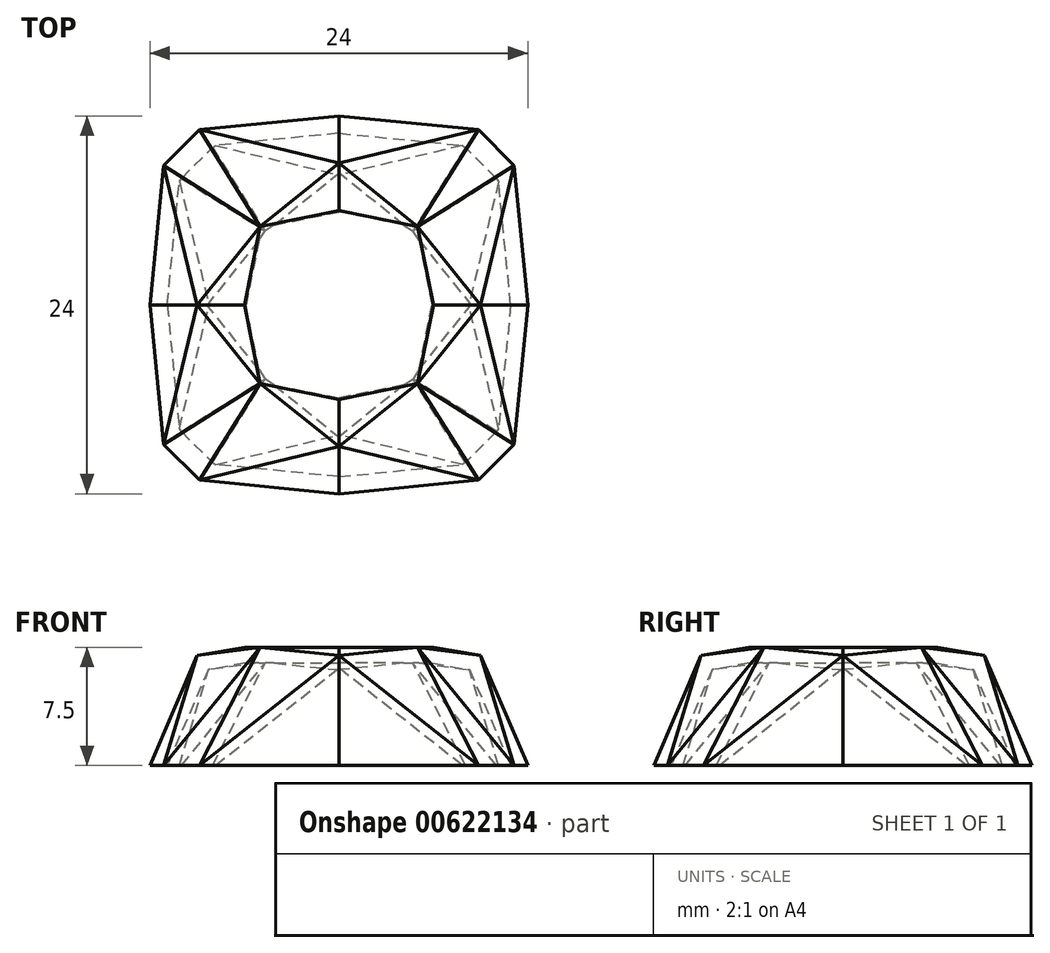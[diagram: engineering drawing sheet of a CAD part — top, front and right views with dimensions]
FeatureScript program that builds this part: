
annotation { "Feature Type Name" : "Feature", "Feature Type Description" : "" }
export const myFeature = defineFeature(function(context is Context, id is Id, definition is map)
    precondition{}
    {
        {
            var Q0;
            Q0=qCreatedBy(makeId("Top.planeOp"),FACE);
            var sketch = newSketch(context, id + "F0", { "sketchPlane" : qUnion([Q0])});
            skLineSegment(sketch, "E0.right", {"start": v(12, 0) * mm, "end": v(12, -12) * mm});
            skLineSegment(sketch, "E1", {"start": v(2, -10) * mm, "end": v(3.15, -11.13) * mm});
            skLineSegment(sketch, "E2", {"start": v(12, -12) * mm, "end": v(3.15, -11.13) * mm});
            skPoint(sketch, "E3.orphan", {"position": v(0, -7.98) * mm});
            skLineSegment(sketch, "E4", {"start": v(12, 0) * mm, "end": v(2, -10) * mm});
            skPoint(sketch, "E5.orphan", {"position": v(0.87, -8.85) * mm});
            skSolve(sketch);
        }
        {
            var Q0;
            Q0=makeQuery(id+"F0.imprint","IMPRINT",FACE,{"disambiguationData":[TD([[makeQuery(id+"F0.imprint","IMPRINT",EDGE,{"derivedFrom":sQuery(id+"F0.wireOp",EDGE,"E0.right")}),-1.0]])]});
            extrude(context, id + "F1", {"entities" : qUnion([Q0]), "depth" : 8.5 * mm, "offsetDistance" : 25.4 * mm});
        }
        {
            var Q0;
            Q0=makeQuery(id+"F1.opExtrude","CAP_FACE",FACE,{"disambiguationData":[OSD([sQuery(id+"F0.wireOp",EDGE,"E0.right"),sQuery(id+"F0.wireOp",EDGE,"E1"),sQuery(id+"F0.wireOp",EDGE,"E2"),sQuery(id+"F0.wireOp",EDGE,"E4")])],"isStart":false});
            var sketch = newSketch(context, id + "F2", { "sketchPlane" : qUnion([Q0])});
            skLineSegment(sketch, "E6", {"start": v(12, 0) * mm, "end": v(7, -5) * mm});
            skLineSegment(sketch, "E7", {"start": v(7, -5) * mm, "end": v(12, -6) * mm});
            skSolve(sketch);
        }
        {
            var Q0;
            {var subQ0=sQuery(id+"F2.wireOp",EDGE,"E6");Q0=makeQuery(id+"F2.imprint","IMPRINT",FACE,{"disambiguationData":[TD([[makeQuery(id+"F2.imprint","IMPRINT",EDGE,{"derivedFrom":subQ0}),1.0]])]});}
            extrude(context, id + "F3", {"entities" : qUnion([Q0]), "operationType" : NewBodyOperationType.REMOVE, "oppositeDirection" : true, "depth" : 1 * mm, "offsetDistance" : 25.4 * mm});
        }
        {
            var Q0;
            Q0=makeQuery(id+"F3.boolean.opBoolean","COPY",EDGE,{"derivedFrom":makeQuery(id+"F3.opExtrude","CAP_EDGE",EDGE,{"disambiguationData":[OSD([sQuery(id+"F2.wireOp",EDGE,"E7")])],"isStart":false})});
            cPlane(context, id + "F4", {"entities" : qUnion([Q0]), "cplaneType" : CPlaneType.LINE_ANGLE, "offset" : 25.4 * mm, "angle" : 100 * degree, "width" : 152.4 * mm, "height" : 152.4 * mm});
        }
        {
            var Q0;
            Q0=qCreatedBy(id+"F4.planeOp",FACE);
            var sketch = newSketch(context, id + "F5", { "sketchPlane" : qUnion([Q0])});
            skLineSegment(sketch, "E8.bottom", {"start": v(-1.53, 1.98) * mm, "end": v(19.8, 1.98) * mm});
            skLineSegment(sketch, "E8.top", {"start": v(-1.53, -14.66) * mm, "end": v(19.8, -14.66) * mm});
            skLineSegment(sketch, "E8.left", {"start": v(-1.53, 1.98) * mm, "end": v(-1.53, -14.66) * mm});
            skLineSegment(sketch, "E8.right", {"start": v(19.8, 1.98) * mm, "end": v(19.8, -14.66) * mm});
            skSolve(sketch);
        }
        {
            var Q0;
            Q0=makeQuery(id+"F5.imprint","IMPRINT",FACE,{"disambiguationData":[TD([[makeQuery(id+"F5.imprint","IMPRINT",EDGE,{"derivedFrom":sQuery(id+"F5.wireOp",EDGE,"E8.bottom")}),-1.0]])]});
            extrude(context, id + "F6", {"entities" : qUnion([Q0]), "operationType" : NewBodyOperationType.REMOVE, "depth" : 25.4 * mm, "offsetDistance" : 25.4 * mm});
        }
        {
            var Q0;
            Q0=makeQuery(id+"F3.boolean.opBoolean","COPY",VERTEX,{"derivedFrom":makeQuery(id+"F3.opExtrude","CAP_VERTEX",VERTEX,{"disambiguationData":[OSD([sQuery(id+"F0.wireOp",EDGE,"E4"),sQuery(id+"F2.wireOp",EDGE,"E6"),sQuery(id+"F2.wireOp",EDGE,"E7")])],"isStart":false})});
            var Q1;
            Q1=makeQuery(id+"F6.boolean.opBoolean","INTERSECT",VERTEX,{"derivedFrom":[makeQuery(id+"F1.opExtrude","SWEPT_FACE",FACE,{"disambiguationData":[OSD([sQuery(id+"F0.wireOp",EDGE,"E2")])]}),makeQuery(id+"F1.opExtrude","SWEPT_FACE",FACE,{"disambiguationData":[OSD([sQuery(id+"F0.wireOp",EDGE,"E0.right")])]}),makeQuery(id+"F6.opExtrude","CAP_FACE",FACE,{"disambiguationData":[OSD([sQuery(id+"F5.wireOp",EDGE,"E8.bottom"),sQuery(id+"F5.wireOp",EDGE,"E8.top"),sQuery(id+"F5.wireOp",EDGE,"E8.left"),sQuery(id+"F5.wireOp",EDGE,"E8.right")])],"isStart":true})]});
            var Q2;
            Q2=makeQuery(id+"F1.opExtrude","CAP_VERTEX",VERTEX,{"disambiguationData":[OSD([sQuery(id+"F0.wireOp",EDGE,"E1"),sQuery(id+"F0.wireOp",EDGE,"E4")])],"isStart":true});
            cPlane(context, id + "F7", {"entities" : qUnion([Q0, Q1, Q2]), "cplaneType" : CPlaneType.THREE_POINT, "offset" : 25.4 * mm, "width" : 152.4 * mm, "height" : 152.4 * mm});
        }
        {
            var Q0;
            Q0=qCreatedBy(id+"F7.planeOp",FACE);
            var sketch = newSketch(context, id + "F8", { "sketchPlane" : qUnion([Q0])});
            skLineSegment(sketch, "E9.bottom", {"start": v(-4.03, 12.86) * mm, "end": v(28.5, 12.86) * mm});
            skLineSegment(sketch, "E9.top", {"start": v(-4.03, -23.7) * mm, "end": v(28.5, -23.7) * mm});
            skLineSegment(sketch, "E9.left", {"start": v(-4.03, 12.86) * mm, "end": v(-4.03, -23.7) * mm});
            skLineSegment(sketch, "E9.right", {"start": v(28.5, 12.86) * mm, "end": v(28.5, -23.7) * mm});
            skSolve(sketch);
        }
        {
            var Q0;
            Q0=makeQuery(id+"F8.imprint","IMPRINT",FACE,{"disambiguationData":[TD([[makeQuery(id+"F8.imprint","IMPRINT",EDGE,{"derivedFrom":sQuery(id+"F8.wireOp",EDGE,"E9.bottom")}),-1.0]])]});
            extrude(context, id + "F9", {"entities" : qUnion([Q0]), "operationType" : NewBodyOperationType.REMOVE, "depth" : 25.4 * mm, "offsetDistance" : 25.4 * mm});
        }
        {
            var Q0;
            Q0=makeQuery(id+"F6.boolean.opBoolean","INTERSECT",EDGE,{"derivedFrom":[makeQuery(id+"F1.opExtrude","SWEPT_FACE",FACE,{"disambiguationData":[OSD([sQuery(id+"F0.wireOp",EDGE,"E0.right")])]}),makeQuery(id+"F6.opExtrude","CAP_FACE",FACE,{"disambiguationData":[OSD([sQuery(id+"F5.wireOp",EDGE,"E8.bottom"),sQuery(id+"F5.wireOp",EDGE,"E8.top"),sQuery(id+"F5.wireOp",EDGE,"E8.left"),sQuery(id+"F5.wireOp",EDGE,"E8.right")])],"isStart":true})]});
            cPoint(context, id + "F10", {"entities" : qUnion([Q0]), "parameter" : 0.5});
        }
        {
            var Q0;
            Q0=makeQuery(id+"F3.boolean.opBoolean","COPY",VERTEX,{"derivedFrom":makeQuery(id+"F3.opExtrude","CAP_VERTEX",VERTEX,{"disambiguationData":[OSD([sQuery(id+"F0.wireOp",EDGE,"E4"),sQuery(id+"F2.wireOp",EDGE,"E6"),sQuery(id+"F2.wireOp",EDGE,"E7")])],"isStart":false})});
            var Q1;
            Q1 = qCreatedBy(id + "F10" ,VERTEX);
            var Q2;
            Q2=makeQuery(id+"F1.opExtrude","CAP_VERTEX",VERTEX,{"disambiguationData":[OSD([sQuery(id+"F0.wireOp",EDGE,"E1"),sQuery(id+"F0.wireOp",EDGE,"E2")])],"isStart":true});
            cPlane(context, id + "F11", {"entities" : qUnion([Q0, Q1, Q2]), "cplaneType" : CPlaneType.THREE_POINT, "offset" : 25.4 * mm, "width" : 152.4 * mm, "height" : 152.4 * mm});
        }
        {
            var Q0;
            Q0=qCreatedBy(id+"F11.planeOp",FACE);
            var sketch = newSketch(context, id + "F12", { "sketchPlane" : qUnion([Q0])});
            skLineSegment(sketch, "E10.bottom", {"start": v(-7.37, 11.71) * mm, "end": v(31.7, 11.71) * mm});
            skLineSegment(sketch, "E10.top", {"start": v(-7.37, -18.88) * mm, "end": v(31.7, -18.88) * mm});
            skLineSegment(sketch, "E10.left", {"start": v(-7.37, 11.71) * mm, "end": v(-7.37, -18.88) * mm});
            skLineSegment(sketch, "E10.right", {"start": v(31.7, 11.71) * mm, "end": v(31.7, -18.88) * mm});
            skSolve(sketch);
        }
        {
            var Q0;
            Q0=makeQuery(id+"F12.imprint","IMPRINT",FACE,{"disambiguationData":[TD([[makeQuery(id+"F12.imprint","IMPRINT",EDGE,{"derivedFrom":sQuery(id+"F12.wireOp",EDGE,"E10.bottom")}),-1.0]])]});
            extrude(context, id + "F13", {"entities" : qUnion([Q0]), "operationType" : NewBodyOperationType.REMOVE, "depth" : 25.4 * mm, "offsetDistance" : 25.4 * mm});
        }
        {
            var Q0;
            Q0=makeQuery(id+"F13.boolean.opBoolean","INTERSECT",VERTEX,{"derivedFrom":[makeQuery(id+"F1.opExtrude","SWEPT_FACE",FACE,{"disambiguationData":[OSD([sQuery(id+"F0.wireOp",EDGE,"E0.right")])]}),makeQuery(id+"F6.boolean.opBoolean","COPY",FACE,{"derivedFrom":makeQuery(id+"F6.opExtrude","CAP_FACE",FACE,{"disambiguationData":[OSD([sQuery(id+"F5.wireOp",EDGE,"E8.bottom"),sQuery(id+"F5.wireOp",EDGE,"E8.top"),sQuery(id+"F5.wireOp",EDGE,"E8.left"),sQuery(id+"F5.wireOp",EDGE,"E8.right")])],"isStart":true})}),makeQuery(id+"F13.opExtrude","CAP_FACE",FACE,{"disambiguationData":[OSD([sQuery(id+"F12.wireOp",EDGE,"E10.bottom"),sQuery(id+"F12.wireOp",EDGE,"E10.top"),sQuery(id+"F12.wireOp",EDGE,"E10.left"),sQuery(id+"F12.wireOp",EDGE,"E10.right")])],"isStart":true})]});
            var Q1;
            Q1=makeQuery(id+"F1.opExtrude","CAP_VERTEX",VERTEX,{"disambiguationData":[OSD([sQuery(id+"F0.wireOp",EDGE,"E0.right"),sQuery(id+"F0.wireOp",EDGE,"E2")])],"isStart":true});
            var Q2;
            Q2=makeQuery(id+"F1.opExtrude","CAP_VERTEX",VERTEX,{"disambiguationData":[OSD([sQuery(id+"F0.wireOp",EDGE,"E1"),sQuery(id+"F0.wireOp",EDGE,"E2")])],"isStart":true});
            cPlane(context, id + "F14", {"entities" : qUnion([Q0, Q1, Q2]), "cplaneType" : CPlaneType.THREE_POINT, "offset" : 25.4 * mm, "width" : 152.4 * mm, "height" : 152.4 * mm});
        }
        {
            var Q0;
            Q0=qCreatedBy(id+"F14.planeOp",FACE);
            var sketch = newSketch(context, id + "F15", { "sketchPlane" : qUnion([Q0])});
            skLineSegment(sketch, "E11.bottom", {"start": v(-4.6, 12.73) * mm, "end": v(29.6, 12.73) * mm});
            skLineSegment(sketch, "E11.top", {"start": v(-4.6, -19.33) * mm, "end": v(29.6, -19.33) * mm});
            skLineSegment(sketch, "E11.left", {"start": v(-4.6, 12.73) * mm, "end": v(-4.6, -19.33) * mm});
            skLineSegment(sketch, "E11.right", {"start": v(29.6, 12.73) * mm, "end": v(29.6, -19.33) * mm});
            skSolve(sketch);
        }
        {
            var Q0;
            Q0=makeQuery(id+"F15.imprint","IMPRINT",FACE,{"disambiguationData":[TD([[makeQuery(id+"F15.imprint","IMPRINT",EDGE,{"derivedFrom":sQuery(id+"F15.wireOp",EDGE,"E11.bottom")}),-1.0]])]});
            extrude(context, id + "F16", {"entities" : qUnion([Q0]), "operationType" : NewBodyOperationType.REMOVE, "depth" : 25.4 * mm, "offsetDistance" : 25.4 * mm});
        }
        {
            var Q0;
            Q0=makeQuery(id+"F3.boolean.opBoolean","COPY",VERTEX,{"derivedFrom":makeQuery(id+"F3.opExtrude","CAP_VERTEX",VERTEX,{"disambiguationData":[OSD([sQuery(id+"F0.wireOp",EDGE,"E4"),sQuery(id+"F2.wireOp",EDGE,"E6"),sQuery(id+"F2.wireOp",EDGE,"E7")])],"isStart":false})});
            var Q1;
            Q1=makeQuery(id+"F1.opExtrude","CAP_VERTEX",VERTEX,{"disambiguationData":[OSD([sQuery(id+"F0.wireOp",EDGE,"E1"),sQuery(id+"F0.wireOp",EDGE,"E4")])],"isStart":true});
            var Q2;
            Q2=makeQuery(id+"F1.opExtrude","CAP_VERTEX",VERTEX,{"disambiguationData":[OSD([sQuery(id+"F0.wireOp",EDGE,"E1"),sQuery(id+"F0.wireOp",EDGE,"E2")])],"isStart":true});
            cPlane(context, id + "F17", {"entities" : qUnion([Q0, Q1, Q2]), "cplaneType" : CPlaneType.THREE_POINT, "offset" : 25.4 * mm, "width" : 152.4 * mm, "height" : 152.4 * mm});
        }
        {
            var Q0;
            Q0=qCreatedBy(id+"F17.planeOp",FACE);
            var sketch = newSketch(context, id + "F18", { "sketchPlane" : qUnion([Q0])});
            skLineSegment(sketch, "E12.bottom", {"start": v(2.6, -6.59) * mm, "end": v(13.1, -6.59) * mm});
            skLineSegment(sketch, "E12.top", {"start": v(2.6, 17.98) * mm, "end": v(13.1, 17.98) * mm});
            skLineSegment(sketch, "E12.left", {"start": v(2.6, -6.59) * mm, "end": v(2.6, 17.98) * mm});
            skLineSegment(sketch, "E12.right", {"start": v(13.1, -6.59) * mm, "end": v(13.1, 17.98) * mm});
            skSolve(sketch);
        }
        {
            var Q0;
            Q0=makeQuery(id+"F18.imprint","IMPRINT",FACE,{"disambiguationData":[TD([[makeQuery(id+"F18.imprint","IMPRINT",EDGE,{"derivedFrom":sQuery(id+"F18.wireOp",EDGE,"E12.bottom")}),1.0]])]});
            extrude(context, id + "F19", {"entities" : qUnion([Q0]), "operationType" : NewBodyOperationType.REMOVE, "oppositeDirection" : true, "depth" : 25.4 * mm, "offsetDistance" : 25.4 * mm});
        }
        {
            var Q0;
            Q0=makeQuery(id+"F1.opExtrude","SWEPT_BODY",BODY,{"disambiguationData":[OSD([sQuery(id+"F0.wireOp",EDGE,"E0.right"),sQuery(id+"F0.wireOp",EDGE,"E1"),sQuery(id+"F0.wireOp",EDGE,"E2"),sQuery(id+"F0.wireOp",EDGE,"E4")])]});
            var Q1;
            Q1=makeQuery(id+"F1.opExtrude","SWEPT_FACE",FACE,{"disambiguationData":[OSD([sQuery(id+"F0.wireOp",EDGE,"E4")])]});
            mirror(context, id + "F20", {"operationType" : NewBodyOperationType.ADD, "entities" : qUnion([Q0]), "mirrorPlane" : qUnion([Q1])});
        }
        {
            var Q0;
            Q0=makeQuery(id+"F1.opExtrude","SWEPT_BODY",BODY,{"disambiguationData":[OSD([sQuery(id+"F0.wireOp",EDGE,"E0.right"),sQuery(id+"F0.wireOp",EDGE,"E1"),sQuery(id+"F0.wireOp",EDGE,"E2"),sQuery(id+"F0.wireOp",EDGE,"E4")])]});
            var Q1;
            Q1=makeQuery(id+"F1.opExtrude","SWEPT_FACE",FACE,{"disambiguationData":[OSD([sQuery(id+"F0.wireOp",EDGE,"E0.right")])]});
            mirror(context, id + "F21", {"operationType" : NewBodyOperationType.ADD, "entities" : qUnion([Q0]), "mirrorPlane" : qUnion([Q1])});
        }
        {
            var Q0;
            Q0=makeQuery(id+"F1.opExtrude","SWEPT_BODY",BODY,{"disambiguationData":[OSD([sQuery(id+"F0.wireOp",EDGE,"E0.right"),sQuery(id+"F0.wireOp",EDGE,"E1"),sQuery(id+"F0.wireOp",EDGE,"E2"),sQuery(id+"F0.wireOp",EDGE,"E4")])]});
            var Q1;
            {var subQ0=makeQuery(id+"F20.opPattern","COPY",FACE,{"derivedFrom":makeQuery(id+"F1.opExtrude","SWEPT_FACE",FACE,{"disambiguationData":[OSD([sQuery(id+"F0.wireOp",EDGE,"E0.right")])]}),"instanceName":"1"});Q1=makeQuery(id+"F21.boolean.opBoolean","MERGE",FACE,{"derivedFrom":[subQ0,makeQuery(id+"F21.opPattern","COPY",FACE,{"derivedFrom":subQ0,"instanceName":"1"})]});}
            mirror(context, id + "F22", {"operationType" : NewBodyOperationType.ADD, "entities" : qUnion([Q0]), "mirrorPlane" : qUnion([Q1])});
        }
        {
            var Q0;
            {var subQ0=makeQuery(id+"F1.opExtrude","CAP_FACE",FACE,{"disambiguationData":[OSD([sQuery(id+"F0.wireOp",EDGE,"E0.right"),sQuery(id+"F0.wireOp",EDGE,"E1"),sQuery(id+"F0.wireOp",EDGE,"E2"),sQuery(id+"F0.wireOp",EDGE,"E4")])],"isStart":true});var subQ1=makeQuery(id+"F20.boolean.opBoolean","MERGE",FACE,{"derivedFrom":[subQ0,makeQuery(id+"F20.opPattern","COPY",FACE,{"derivedFrom":subQ0,"instanceName":"1"})]});var subQ2=makeQuery(id+"F21.boolean.opBoolean","MERGE",FACE,{"derivedFrom":[subQ1,makeQuery(id+"F21.opPattern","COPY",FACE,{"derivedFrom":subQ1,"instanceName":"1"})]});Q0=makeQuery(id+"F22.boolean.opBoolean","MERGE",FACE,{"derivedFrom":[subQ2,makeQuery(id+"F22.opPattern","COPY",FACE,{"derivedFrom":subQ2,"instanceName":"1"})]});}
            shell(context, id + "F23", {"entities" : qUnion([Q0]), "thickness" : 1 * mm});
        }
    });
